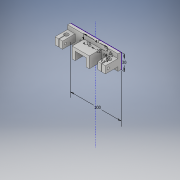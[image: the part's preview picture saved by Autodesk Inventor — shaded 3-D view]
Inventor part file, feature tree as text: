
AUTODESK INVENTOR PART (.ipt)
format: ipt  version: 2019 (Build 230136000, 136)  size: 370,176 bytes
history: native  units: in
note: dims shown in document units (in); Inventor stores cm internally (conversion verified against a paired STEP export)
features: extrude x7, sketch x6
ambient origin geometry x8: Origin, YZ Plane, XZ Plane, XY Plane, X Axis, Y Axis, Z Axis, Center Point
bodies: Solid1 (feature_tree)
feature tree (13):
  sketch  "Sketch1"  dims[d1=1.1811in d2=3.937in]
  extrude  "Extrusion1"  Depth=3.937in
  extrude  "Extrusion2"  Depth=0.2362in
  extrude  "Extrusion3"  Depth=0.2362in
  extrude  "Extrusion4"  Depth=1.1811in TaperAngle=0.0deg
  extrude  "Extrusion5"  Depth=0.1673in
  extrude  "Extrusion6"  Depth=0.3937in
  extrude  "Extrusion7"  Depth=1.1811in TaperAngle=0.0deg
  sketch  "Sketch2"  dims[d3=0.8661in d4=0.2362in]
  sketch  "Sketch3"  dims[d5=0.6299in d6=0.2362in]
  sketch  "Sketch4"  dims[d7=0.2362in d8=0.0in d9=1.1811in d10=0.0in]
  sketch  "Sketch5"  dims[d11=0.1673in d13=0.1673in]
  sketch  "Sketch6"  dims[d14=0.1673in d15=0.4724in d16=1.1811in d17=0.0in d18=1.8504in d19=0.5906in d20=0.5512in d21=0.9843in d22=0.0in d23=0.315in d24=0.6299in d25=0.0394in d26=0.315in d27=0.0394in d28=1.1811in d29=0.0in d30=0.1673in d32=1.1811in d33=0.0in d34=0.3937in d35=0.0in]
